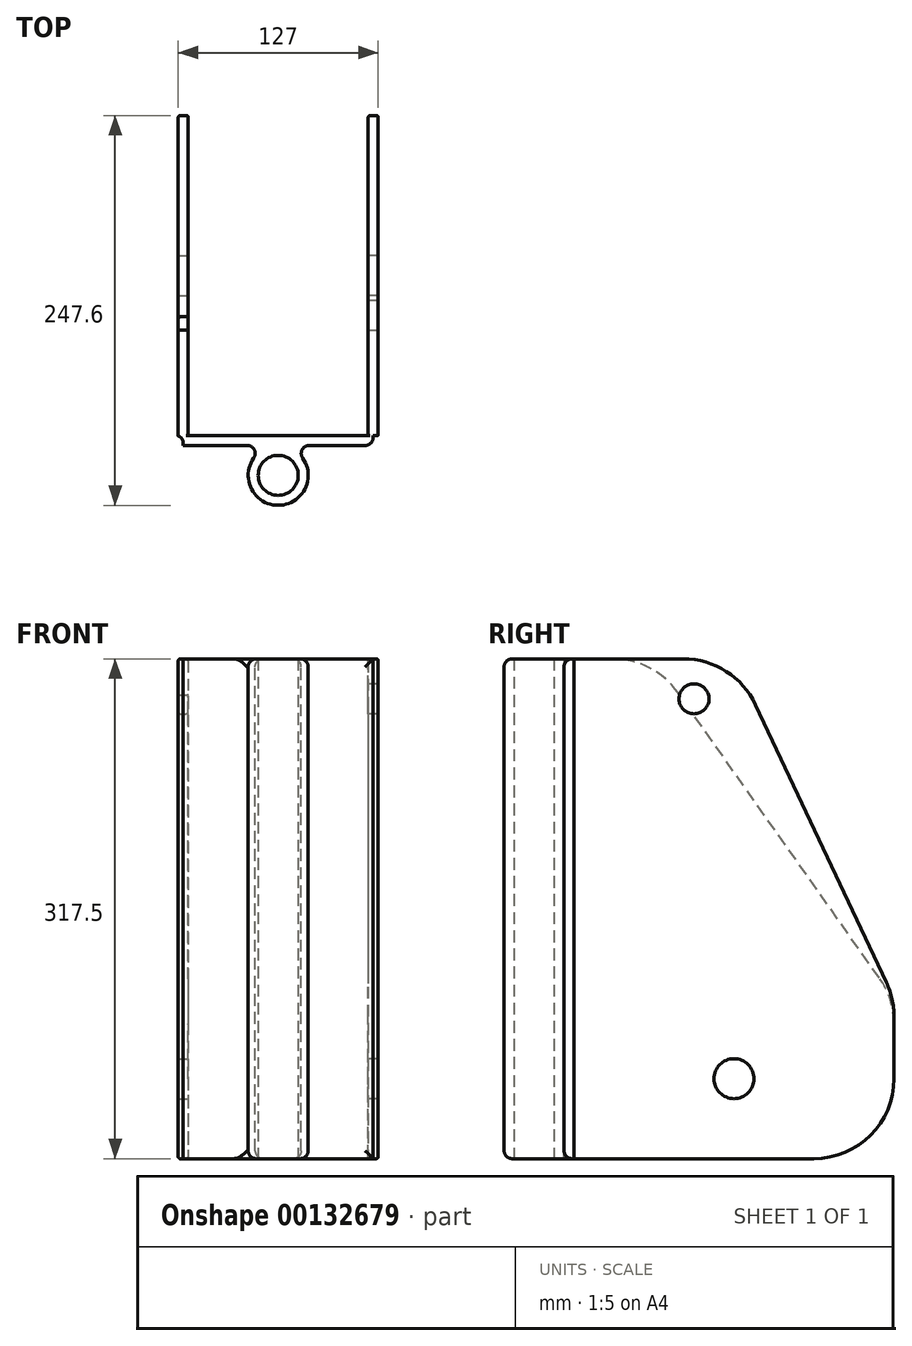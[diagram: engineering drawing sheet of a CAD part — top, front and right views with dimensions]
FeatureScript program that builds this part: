
annotation { "Feature Type Name" : "Feature", "Feature Type Description" : "" }
export const myFeature = defineFeature(function(context is Context, id is Id, definition is map)
    precondition{}
    {
        {
            var Q0;
            Q0=qCreatedBy(makeId("Right.planeOp"),FACE);
            var sketch = newSketch(context, id + "F0", { "sketchPlane" : qUnion([Q0])});
            skLineSegment(sketch, "E0", {"start": v(-76.2, 139.7) * mm, "end": v(-76.2, -177.8) * mm});
            skLineSegment(sketch, "E1", {"start": v(-76.2, -177.8) * mm, "end": v(127, -177.8) * mm});
            skLineSegment(sketch, "E2", {"start": v(127, -177.8) * mm, "end": v(127, -76.2) * mm});
            skLineSegment(sketch, "E3", {"start": v(-76.2, 139.7) * mm, "end": v(25.4, 139.68) * mm});
            skLineSegment(sketch, "E4", {"start": v(25.4, 139.68) * mm, "end": v(127, -76.2) * mm});
            skCircle(sketch, "E5", {"center": v(25.4, -127) * mm, "radius": 12.7 * mm});
            skPoint(sketch, "E5.centerSnap0", {"position": v(127, -127) * mm});
            skCircle(sketch, "E6", {"center": v(0, 114.28) * mm, "radius": 9.53 * mm});
            skSolve(sketch);
        }
        {
            var Q0;
            Q0=makeQuery(id+"F0.imprint","IMPRINT",FACE,{"disambiguationData":[TD([[makeQuery(id+"F0.imprint","IMPRINT",EDGE,{"derivedFrom":sQuery(id+"F0.wireOp",EDGE,"E0")}),1.0]])]});
            extrude(context, id + "F1", {"entities" : qUnion([Q0]), "depth" : 6.35 * mm});
        }
        {
            var Q0;
            Q0=makeQuery(id+"F1.opExtrude","SWEPT_FACE",FACE,{"disambiguationData":[OSD([sQuery(id+"F0.wireOp",EDGE,"E0")])]});
            var sketch = newSketch(context, id + "F2", { "sketchPlane" : qUnion([Q0])});
            skLineSegment(sketch, "E7.bottom", {"start": v(3.17, 139.7) * mm, "end": v(-117.48, 139.7) * mm});
            skLineSegment(sketch, "E7.top", {"start": v(3.18, -177.8) * mm, "end": v(-117.47, -177.8) * mm});
            skLineSegment(sketch, "E7.left", {"start": v(3.18, 139.7) * mm, "end": v(3.18, -177.8) * mm});
            skLineSegment(sketch, "E7.right", {"start": v(-117.48, 139.7) * mm, "end": v(-117.47, -177.8) * mm});
            skSolve(sketch);
        }
        {
            var Q0;
            {var subQ2=sQuery(id+"F2.wireOp",EDGE,"E7.right");Q0=makeQuery(id+"F2.imprint","IMPRINT",FACE,{"disambiguationData":[TD([[makeQuery(id+"F2.imprint","IMPRINT",EDGE,{"derivedFrom":subQ2}),1.0]])]});}
            var Q1;
            {var subQ3=sQuery(id+"F2.wireOp",EDGE,"E7.left");Q1=makeQuery(id+"F2.imprint","IMPRINT",FACE,{"disambiguationData":[TD([[makeQuery(id+"F2.imprint","IMPRINT",EDGE,{"derivedFrom":subQ3}),-1.0]])]});}
            extrude(context, id + "F3", {"entities" : qUnion([Q0, Q1]), "operationType" : NewBodyOperationType.ADD, "depth" : 6.35 * mm});
        }
        {
            var Q0;
            Q0=makeQuery(id+"F3.opExtrude","SWEPT_FACE",FACE,{"disambiguationData":[OSD([sQuery(id+"F2.wireOp",EDGE,"E7.right")])]});
            var sketch = newSketch(context, id + "F4", { "sketchPlane" : qUnion([Q0])});
            skLineSegment(sketch, "E8", {"start": v(76.19, 139.7) * mm, "end": v(25.39, 139.7) * mm});
            skLineSegment(sketch, "E9", {"start": v(76.19, 139.7) * mm, "end": v(76.2, -177.8) * mm});
            skLineSegment(sketch, "E10", {"start": v(76.2, -177.8) * mm, "end": v(-127, -177.8) * mm});
            skLineSegment(sketch, "E11", {"start": v(-127, -177.8) * mm, "end": v(-127, -76.2) * mm});
            skLineSegment(sketch, "E12", {"start": v(-127, -76.2) * mm, "end": v(25.39, 139.7) * mm});
            skCircle(sketch, "E13", {"center": v(0, 114.28) * mm, "radius": 9.53 * mm});
            skCircle(sketch, "E14", {"center": v(-25.4, -127) * mm, "radius": 12.7 * mm});
            skSolve(sketch);
        }
        {
            var Q0;
            Q0=makeQuery(id+"F4.imprint","IMPRINT",FACE,{"disambiguationData":[TD([[makeQuery(id+"F4.imprint","IMPRINT",EDGE,{"derivedFrom":sQuery(id+"F4.wireOp",EDGE,"E8")}),1.0]])]});
            extrude(context, id + "F5", {"entities" : qUnion([Q0]), "operationType" : NewBodyOperationType.ADD, "depth" : 3.17 * mm, "hasSecondDirection" : true, "secondDirectionOppositeDirection" : true, "secondDirectionDepth" : 3.17 * mm});
        }
        {
            var Q0;
            Q0=makeQuery(id+"F5.opExtrude","SWEPT_FACE",FACE,{"disambiguationData":[OSD([sQuery(id+"F4.wireOp",EDGE,"E9")])]});
            var Q1;
            Q1=makeQuery(id+"F1.opExtrude","SWEPT_BODY",BODY,{"disambiguationData":[OSD([sQuery(id+"F0.wireOp",EDGE,"E0"),sQuery(id+"F0.wireOp",EDGE,"E1"),sQuery(id+"F0.wireOp",EDGE,"E2"),sQuery(id+"F0.wireOp",EDGE,"E3"),sQuery(id+"F0.wireOp",EDGE,"E4"),sQuery(id+"F0.wireOp",EDGE,"E5"),sQuery(id+"F0.wireOp",EDGE,"E6")])]});
            extrude(context, id + "F6", {"entities" : qUnion([Q0]), "operationType" : NewBodyOperationType.ADD, "endBoundEntityBody" : qUnion([Q1]), "depth" : 0.25 * mm});
        }
        {
            var Q0;
            Q0=makeQuery(id+"F6.boolean.opBoolean","INTERSECT",EDGE,{"derivedFrom":[makeQuery(id+"F3.opExtrude","SWEPT_FACE",FACE,{"disambiguationData":[OSD([sQuery(id+"F2.wireOp",EDGE,"E7.right")])]}),makeQuery(id+"F6.opExtrude","CAP_FACE",FACE,{"disambiguationData":[OSD([sQuery(id+"F4.wireOp",EDGE,"E9")])],"isStart":false})]});
            var Q1;
            Q1=makeQuery(id+"F3.opExtrude","CAP_EDGE",EDGE,{"disambiguationData":[OSD([sQuery(id+"F2.wireOp",EDGE,"E7.left")])],"isStart":true});
            fillet(context, id + "F7", {"entities" : qUnion([Q0, Q1]), "radius" : 5.08 * mm, "tangentPropagation" : true, "allowEdgeOverflow" : false});
        }
        {
            var Q0;
            Q0=makeQuery(id+"F5.opExtrude","SWEPT_EDGE",EDGE,{"disambiguationData":[OSD([sQuery(id+"F4.wireOp",EDGE,"E8"),sQuery(id+"F4.wireOp",EDGE,"E12")])]});
            var Q1;
            Q1=makeQuery(id+"F1.opExtrude","SWEPT_EDGE",EDGE,{"disambiguationData":[OSD([sQuery(id+"F0.wireOp",EDGE,"E3"),sQuery(id+"F0.wireOp",EDGE,"E4")])]});
            var Q2;
            Q2=makeQuery(id+"F1.opExtrude","SWEPT_EDGE",EDGE,{"disambiguationData":[OSD([sQuery(id+"F0.wireOp",EDGE,"E2"),sQuery(id+"F0.wireOp",EDGE,"E4")])]});
            var Q3;
            Q3=makeQuery(id+"F5.opExtrude","SWEPT_EDGE",EDGE,{"disambiguationData":[OSD([sQuery(id+"F4.wireOp",EDGE,"E11"),sQuery(id+"F4.wireOp",EDGE,"E12")])]});
            var Q4;
            Q4=makeQuery(id+"F5.opExtrude","SWEPT_EDGE",EDGE,{"disambiguationData":[OSD([sQuery(id+"F4.wireOp",EDGE,"E10"),sQuery(id+"F4.wireOp",EDGE,"E11")])]});
            var Q5;
            Q5=makeQuery(id+"F1.opExtrude","SWEPT_EDGE",EDGE,{"disambiguationData":[OSD([sQuery(id+"F0.wireOp",EDGE,"E1"),sQuery(id+"F0.wireOp",EDGE,"E2")])]});
            fillet(context, id + "F8", {"entities" : qUnion([Q0, Q1, Q2, Q3, Q4, Q5]), "radius" : 50.8 * mm, "tangentPropagation" : true, "allowEdgeOverflow" : false});
        }
        {
            var Q0;
            Q0=makeQuery(id+"F1.opExtrude","CAP_EDGE",EDGE,{"disambiguationData":[OSD([sQuery(id+"F0.wireOp",EDGE,"E4")])],"isStart":false});
            var Q1;
            Q1=makeQuery(id+"F1.opExtrude","CAP_EDGE",EDGE,{"disambiguationData":[OSD([sQuery(id+"F0.wireOp",EDGE,"E4")])],"isStart":true});
            var Q2;
            Q2=makeQuery(id+"F5.opExtrude","CAP_EDGE",EDGE,{"disambiguationData":[OSD([sQuery(id+"F4.wireOp",EDGE,"E12")])],"isStart":true});
            var Q3;
            Q3=makeQuery(id+"F5.opExtrude","CAP_EDGE",EDGE,{"disambiguationData":[OSD([sQuery(id+"F4.wireOp",EDGE,"E12")])],"isStart":false});
            fillet(context, id + "F9", {"entities" : qUnion([Q0, Q1, Q2, Q3]), "radius" : 1.27 * mm, "tangentPropagation" : true, "allowEdgeOverflow" : false});
        }
        {
            var Q0;
            Q0=makeQuery(id+"F3.opExtrude","SWEPT_FACE",FACE,{"disambiguationData":[OSD([sQuery(id+"F2.wireOp",EDGE,"E7.bottom")])]});
            var sketch = newSketch(context, id + "F10", { "sketchPlane" : qUnion([Q0])});
            skCircle(sketch, "E15", {"center": v(-57.15, -101.55) * mm, "radius": 19.05 * mm});
            skPoint(sketch, "E16", {"position": v(-57.15, -82.55) * mm});
            skSolve(sketch);
        }
        {
            var Q0;
            {var subQ0=sQuery(id+"F10.wireOp",EDGE,"E15");var subQ1=makeQuery(id+"F3.opExtrude","CAP_EDGE",EDGE,{"disambiguationData":[OSD([sQuery(id+"F2.wireOp",EDGE,"E7.bottom")])],"isStart":false});var subQ2=makeQuery(id+"F10.imprint","INTERSECT",VERTEX,{"disambiguationData":[OD(0.0)],"derivedFrom":[subQ1,subQ0]});Q0=makeQuery(id+"F10.imprint","IMPRINT",FACE,{"disambiguationData":[TD([[makeQuery(id+"F10.imprint","IMPRINT",EDGE,{"disambiguationData":[TD([[subQ2,1.0]])],"derivedFrom":subQ0}),1.0]])]});}
            extrude(context, id + "F11", {"entities" : qUnion([Q0]), "operationType" : NewBodyOperationType.ADD, "oppositeDirection" : true, "depth" : 317.5 * mm});
        }
        {
            var Q0;
            {var subQ0=sQuery(id+"F2.wireOp",EDGE,"E7.bottom");Q0=makeQuery(id+"F11.boolean.opBoolean","MERGE",FACE,{"derivedFrom":[makeQuery(id+"F3.opExtrude","SWEPT_FACE",FACE,{"disambiguationData":[OSD([subQ0])]}),makeQuery(id+"F11.opExtrude","CAP_FACE",FACE,{"disambiguationData":[OSD([subQ0,sQuery(id+"F10.wireOp",EDGE,"E15")])],"isStart":true})]});}
            var sketch = newSketch(context, id + "F12", { "sketchPlane" : qUnion([Q0])});
            skPoint(sketch, "E17", {"position": v(-57.15, -101.55) * mm});
            skSolve(sketch);
        }
        {
            var Q0;
            Q0=sQuery(id+"F12.wireOp",VERTEX,"E17");
            var Q1;
            Q1=makeQuery(id+"F1.opExtrude","SWEPT_BODY",BODY,{"disambiguationData":[OSD([sQuery(id+"F0.wireOp",EDGE,"E0"),sQuery(id+"F0.wireOp",EDGE,"E1"),sQuery(id+"F0.wireOp",EDGE,"E2"),sQuery(id+"F0.wireOp",EDGE,"E3"),sQuery(id+"F0.wireOp",EDGE,"E4"),sQuery(id+"F0.wireOp",EDGE,"E5"),sQuery(id+"F0.wireOp",EDGE,"E6")])]});
            hole(context, id + "F13", {"style" : HoleStyle.SIMPLE, "endStyle" : HoleEndStyle.THROUGH, "holeDiameter" : 25.4 * mm, "startFromSketch" : true, "locations" : qUnion([Q0]), "scope" : qUnion([Q1]), "isTappedThrough" : true});
        }
        {
            var Q0;
            {var subQ0=sQuery(id+"F2.wireOp",EDGE,"E7.left");var subQ2=sQuery(id+"F2.wireOp",EDGE,"E7.bottom");var subQ3=sQuery(id+"F2.wireOp",EDGE,"E7.top");Q0=makeQuery(id+"F11.boolean.opBoolean","SPLIT",FACE,{"disambiguationData":[TD([makeQuery(id+"F3.opExtrude","SWEPT_FACE",FACE,{"disambiguationData":[OSD([subQ0])]})])],"derivedFrom":makeQuery(id+"F3.opExtrude","CAP_FACE",FACE,{"disambiguationData":[OSD([subQ2,subQ3,subQ0,sQuery(id+"F2.wireOp",EDGE,"E7.right")])],"isStart":false})});}
            var Q1;
            Q1=makeQuery(id+"F11.opExtrude","SWEPT_FACE",FACE,{"disambiguationData":[OSD([sQuery(id+"F10.wireOp",EDGE,"E15")])]});
            fillet(context, id + "F14", {"entities" : qUnion([Q0, Q1]), "radius" : 5.08 * mm, "tangentPropagation" : true, "allowEdgeOverflow" : false});
        }
    });
